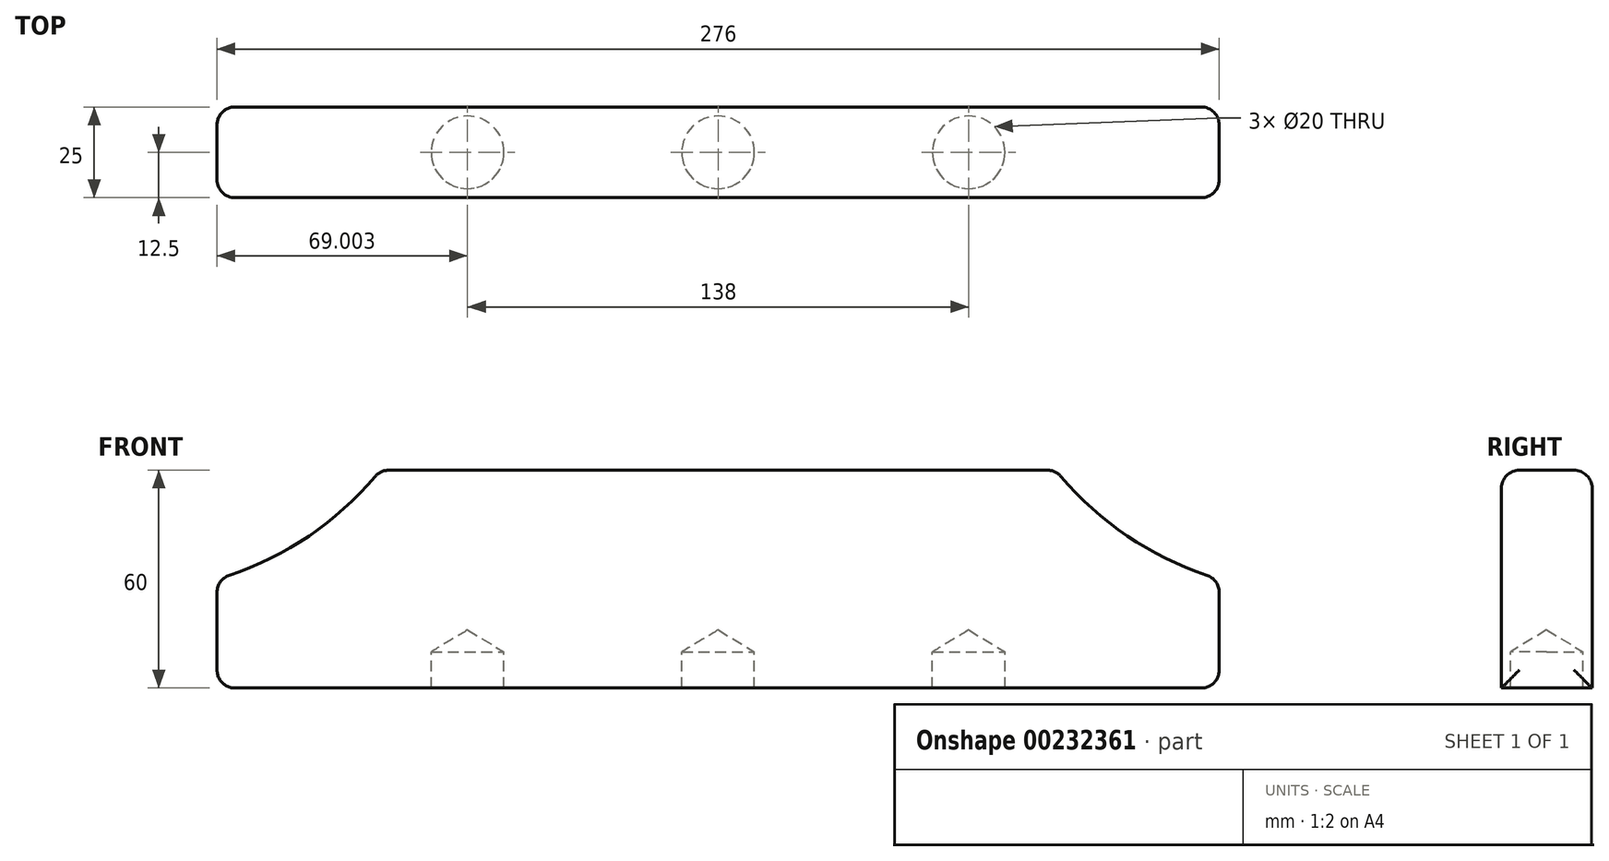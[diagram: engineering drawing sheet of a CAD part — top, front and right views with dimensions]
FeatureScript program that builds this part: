
annotation { "Feature Type Name" : "Feature", "Feature Type Description" : "" }
export const myFeature = defineFeature(function(context is Context, id is Id, definition is map)
    precondition{}
    {
        {
            var Q0;
            Q0=qCreatedBy(makeId("Front.planeOp"),FACE);
            var sketch = newSketch(context, id + "F0", { "sketchPlane" : qUnion([Q0])});
            skLineSegment(sketch, "E0", {"start": v(-135.86, 0) * mm, "end": v(140.14, 0) * mm});
            skLineSegment(sketch, "E1", {"start": v(140.14, 0) * mm, "end": v(140.14, 30) * mm});
            skLineSegment(sketch, "E2", {"start": v(95.14, 60) * mm, "end": v(-90.86, 60) * mm});
            skLineSegment(sketch, "E3", {"start": v(-135.86, 30) * mm, "end": v(-135.86, 0) * mm});
            skArc(sketch, "E4", {"start": v(-135.86, 30) * mm, "mid": v(-111.05, 41.54) * mm, "end": v(-90.86, 60) * mm});
            skArc(sketch, "E5", {"start": v(95.14, 60) * mm, "mid": v(115.34, 41.54) * mm, "end": v(140.14, 30) * mm});
            skSolve(sketch);
        }
        {
            var Q0;
            Q0 = qSketchRegion(id + "F0", true);
            extrude(context, id + "F1", {"entities" : qUnion([Q0]), "oppositeDirection" : true, "depth" : 25 * mm});
        }
        {
            var Q0;
            Q0=qCreatedBy(makeId("Top.planeOp"),FACE);
            var sketch = newSketch(context, id + "F2", { "sketchPlane" : qUnion([Q0])});
            skCircle(sketch, "E6", {"center": v(2.14, 12.5) * mm, "radius": 10 * mm});
            skCircle(sketch, "E7.1.0.0", {"center": v(71.14, 12.5) * mm, "radius": 10 * mm});
            skLineSegment(sketch, "E7.direction1", {"start": v(2.14, 12.5) * mm, "end": v(71.14, 12.5) * mm, "construction": true});
            skCircle(sketch, "E8.1.0.0", {"center": v(-66.86, 12.5) * mm, "radius": 10 * mm});
            skLineSegment(sketch, "E8.direction1", {"start": v(2.14, 12.5) * mm, "end": v(-66.86, 12.5) * mm, "construction": true});
            skSolve(sketch);
        }
        {
            var Q0;
            Q0=sQuery(id+"F2.wireOp",VERTEX,"E8.1.0.0.center");
            var Q1;
            Q1=sQuery(id+"F2.wireOp",VERTEX,"E6.center");
            var Q2;
            Q2=sQuery(id+"F2.wireOp",VERTEX,"E7.direction1.end");
            var Q3;
            Q3=makeQuery(id+"F1.opExtrude","SWEPT_BODY",BODY,{"disambiguationData":[OSD([sQuery(id+"F0.wireOp",EDGE,"E0"),sQuery(id+"F0.wireOp",EDGE,"E1"),sQuery(id+"F0.wireOp",EDGE,"E2"),sQuery(id+"F0.wireOp",EDGE,"E3"),sQuery(id+"F0.wireOp",EDGE,"E4"),sQuery(id+"F0.wireOp",EDGE,"E5")])]});
            hole(context, id + "F3", {"style" : HoleStyle.SIMPLE, "endStyle" : HoleEndStyle.BLIND, "oppositeDirection" : true, "holeDiameter" : 20 * mm, "holeDepth" : 10 * mm, "locations" : qUnion([Q0, Q1, Q2]), "scope" : qUnion([Q3]), "startStyle" : HoleStartStyle.SKETCH});
        }
        {
            var Q0;
            Q0=makeQuery(id+"F1.opExtrude","SWEPT_FACE",FACE,{"disambiguationData":[OSD([sQuery(id+"F0.wireOp",EDGE,"E1")])]});
            var Q1;
            Q1=makeQuery(id+"F1.opExtrude","SWEPT_FACE",FACE,{"disambiguationData":[OSD([sQuery(id+"F0.wireOp",EDGE,"E3")])]});
            var Q2;
            Q2=makeQuery(id+"F1.opExtrude","SWEPT_FACE",FACE,{"disambiguationData":[OSD([sQuery(id+"F0.wireOp",EDGE,"E4")])]});
            var Q3;
            Q3=makeQuery(id+"F1.opExtrude","SWEPT_FACE",FACE,{"disambiguationData":[OSD([sQuery(id+"F0.wireOp",EDGE,"E2")])]});
            var Q4;
            Q4=makeQuery(id+"F1.opExtrude","SWEPT_FACE",FACE,{"disambiguationData":[OSD([sQuery(id+"F0.wireOp",EDGE,"E5")])]});
            fillet(context, id + "F4", {"entities" : qUnion([Q0, Q1, Q2, Q3, Q4]), "radius" : 5 * mm, "tangentPropagation" : true, "allowEdgeOverflow" : false});
        }
    });
